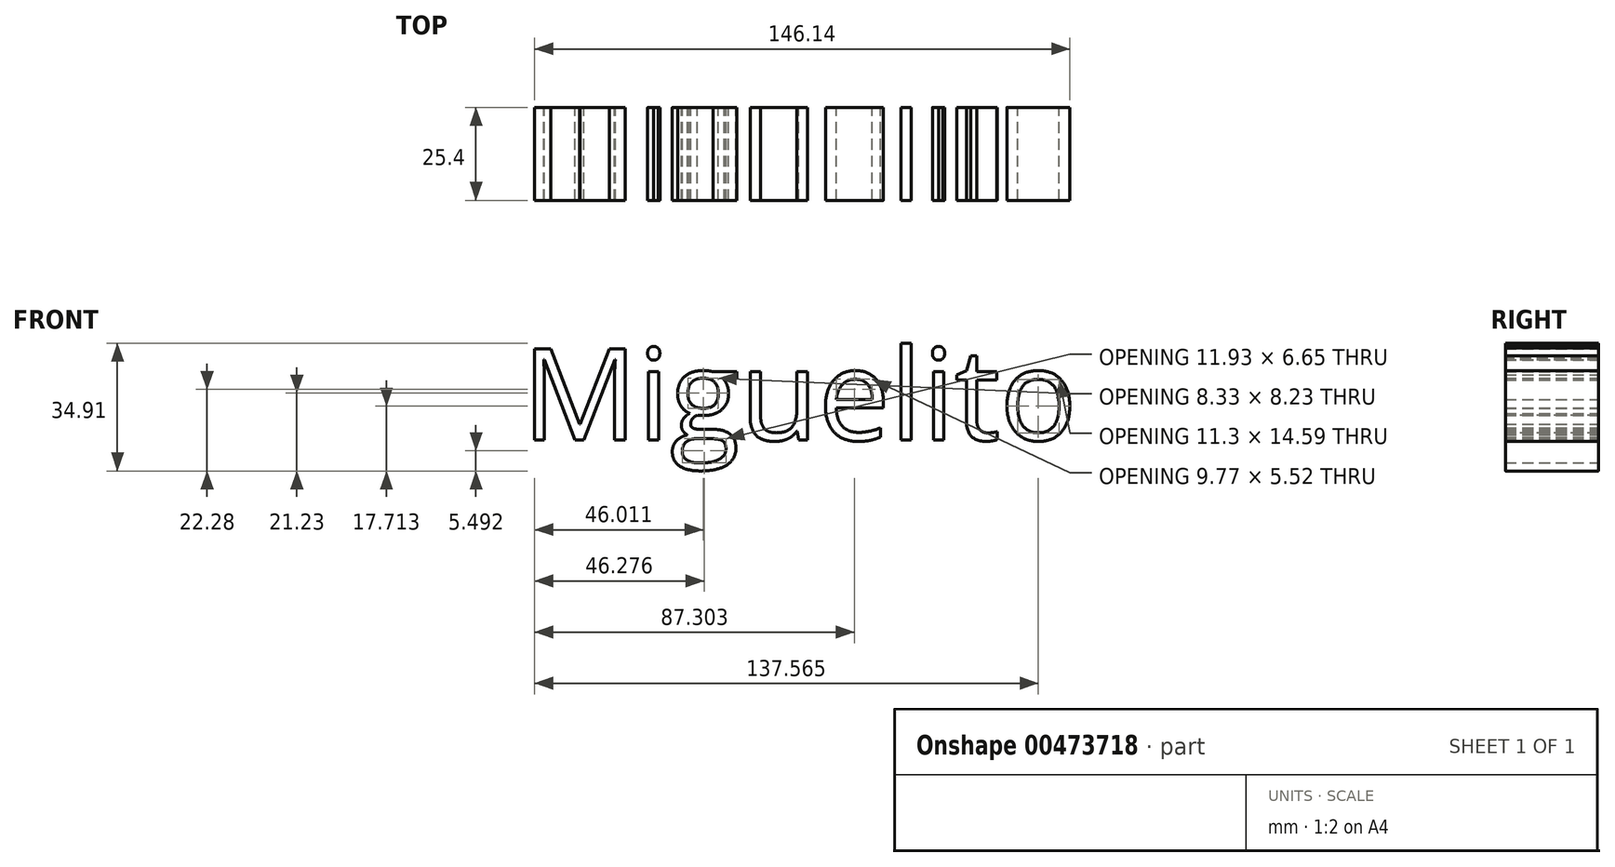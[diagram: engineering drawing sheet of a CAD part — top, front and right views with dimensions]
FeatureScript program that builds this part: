
annotation { "Feature Type Name" : "Feature", "Feature Type Description" : "" }
export const myFeature = defineFeature(function(context is Context, id is Id, definition is map)
    precondition{}
    {
        {
            var Q0;
            Q0=qCreatedBy(makeId("Front.planeOp"),FACE);
            var sketch = newSketch(context, id + "F0", { "sketchPlane" : qUnion([Q0])});
            skText(sketch, "E0", { "text": "Miguelito", "fontName": "OpenSans-Regular.ttf"});
            const initialGuessF0  = {"E0": [-0.07574, 0.0153, 1, 0, 0.02513]};
            skSetInitialGuess(sketch, initialGuessF0);
            skSolve(sketch);
        }
        {
            var Q0;
            Q0 = qSketchRegion(id + "F0", true);
            extrude(context, id + "F1", {"entities" : qUnion([Q0]), "depth" : 25.4 * mm});
        }
    });
